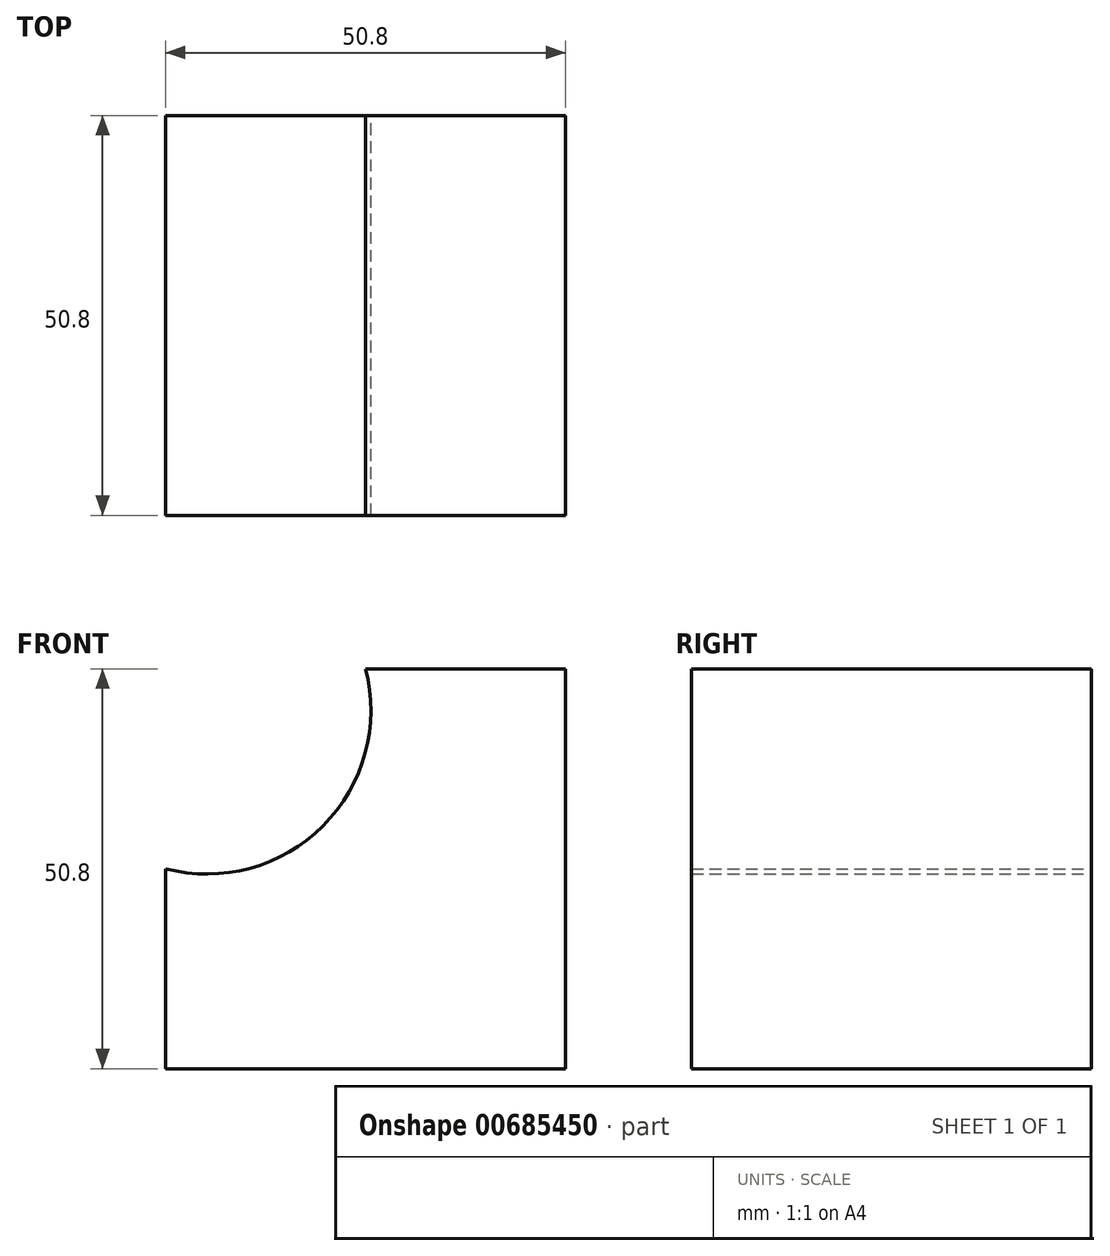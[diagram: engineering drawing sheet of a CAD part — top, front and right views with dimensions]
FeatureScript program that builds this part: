
annotation { "Feature Type Name" : "Feature", "Feature Type Description" : "" }
export const myFeature = defineFeature(function(context is Context, id is Id, definition is map)
    precondition{}
    {
        {
            var Q0;
            Q0=qCreatedBy(makeId("Front.planeOp"),FACE);
            var sketch = newSketch(context, id + "F0", { "sketchPlane" : qUnion([Q0])});
            skLineSegment(sketch, "E0", {"start": v(0, 0) * mm, "end": v(0, 50.8) * mm});
            skLineSegment(sketch, "E1", {"start": v(0, 0) * mm, "end": v(-50.8, 0) * mm});
            skLineSegment(sketch, "E2", {"start": v(0, 50.8) * mm, "end": v(-25.4, 50.8) * mm});
            skLineSegment(sketch, "E3", {"start": v(-50.8, 0) * mm, "end": v(-50.8, 25.4) * mm});
            skArc(sketch, "E4", {"start": v(-50.8, 25.4) * mm, "mid": v(-30.82, 30.82) * mm, "end": v(-25.4, 50.8) * mm});
            skSolve(sketch);
        }
        {
            var Q0;
            Q0 = qSketchRegion(id + "F0", true);
            extrude(context, id + "F1", {"entities" : qUnion([Q0]), "depth" : 50.8 * mm, "offsetDistance" : 25.4 * mm});
        }
    });
